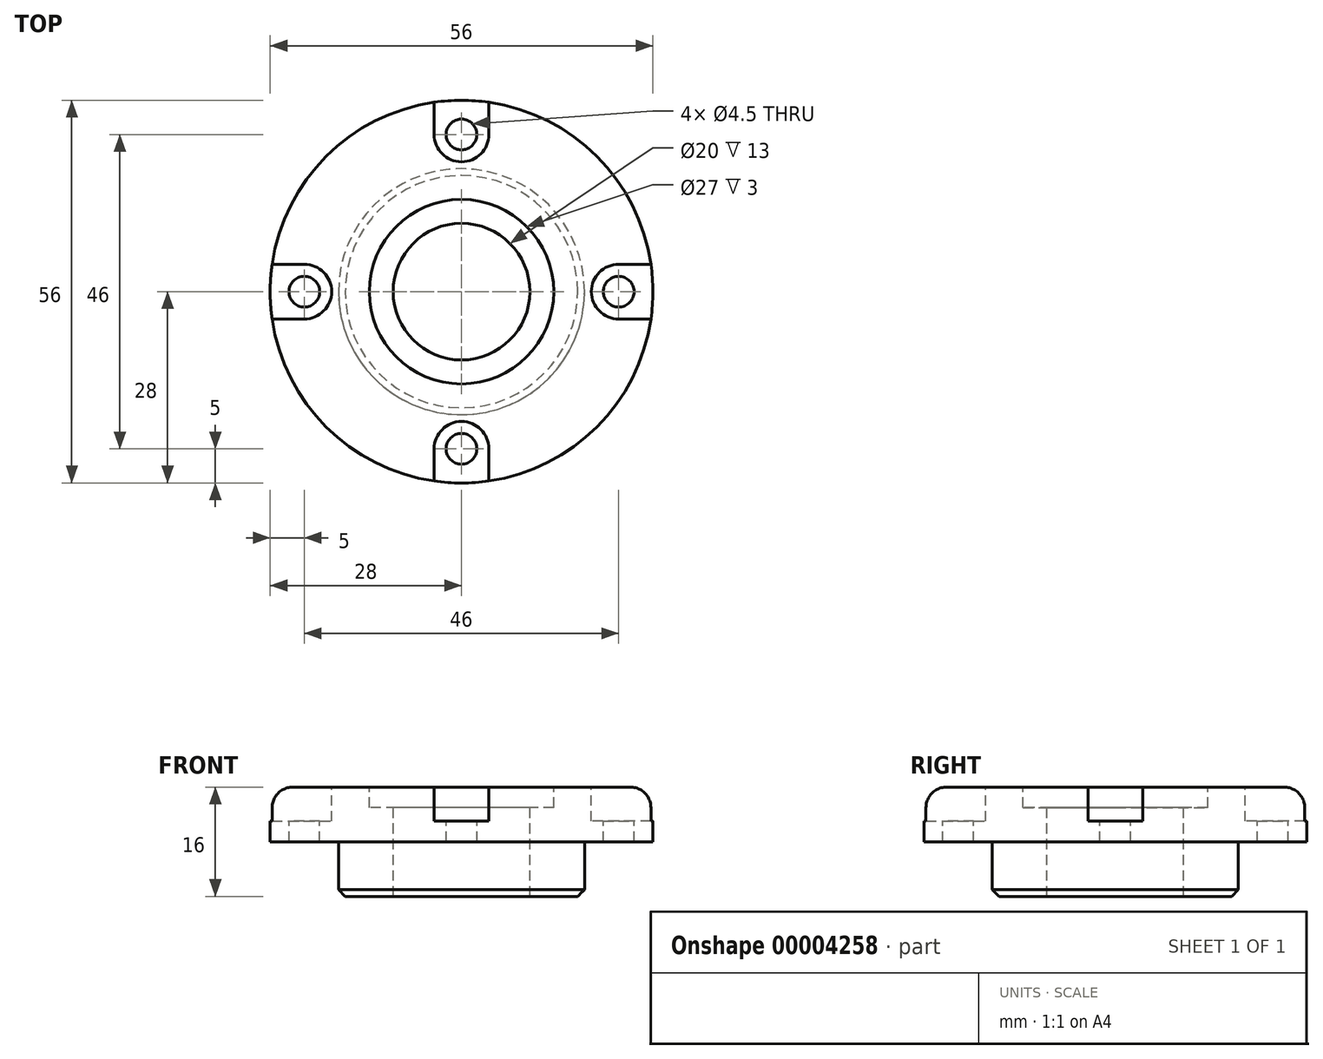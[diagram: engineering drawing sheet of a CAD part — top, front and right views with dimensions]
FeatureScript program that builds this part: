
annotation { "Feature Type Name" : "Feature", "Feature Type Description" : "" }
export const myFeature = defineFeature(function(context is Context, id is Id, definition is map)
    precondition{}
    {
        {
            var Q0;
            Q0=qCreatedBy(makeId("Front.planeOp"),FACE);
            var sketch = newSketch(context, id + "F0", { "sketchPlane" : qUnion([Q0])});
            skLineSegment(sketch, "E0", {"start": v(0, 0) * mm, "end": v(0, 33.62) * mm, "construction": true});
            skLineSegment(sketch, "E1", {"start": v(0, 16) * mm, "end": v(28, 16) * mm});
            skLineSegment(sketch, "E2", {"start": v(28, 16) * mm, "end": v(28, 8) * mm});
            skLineSegment(sketch, "E3", {"start": v(28, 8) * mm, "end": v(18, 8) * mm});
            skLineSegment(sketch, "E4", {"start": v(18, 8) * mm, "end": v(18, 0) * mm});
            skLineSegment(sketch, "E5", {"start": v(18, 0) * mm, "end": v(0, 0) * mm});
            skLineSegment(sketch, "E6", {"start": v(0, 16) * mm, "end": v(0, 0) * mm});
            skSolve(sketch);
        }
        {
            var Q0;
            Q0 = qSketchRegion(id + "F0", true);
            var Q1;
            Q1=sQuery(id+"F0.wireOp",EDGE,"E0");
            revolve(context, id + "F1", {"entities" : qUnion([Q0]), "axis" : qUnion([Q1]), "revolveType" : RevolveType.FULL});
        }
        {
            var Q0;
            Q0=qCreatedBy(makeId("Front.planeOp"),FACE);
            var sketch = newSketch(context, id + "F2", { "sketchPlane" : qUnion([Q0])});
            skLineSegment(sketch, "E7", {"start": v(0, 0) * mm, "end": v(0, 20.28) * mm, "construction": true});
            skLineSegment(sketch, "E8", {"start": v(0, 16) * mm, "end": v(13.5, 16) * mm});
            skLineSegment(sketch, "E9", {"start": v(13.5, 16) * mm, "end": v(13.5, 13) * mm});
            skLineSegment(sketch, "E10", {"start": v(13.5, 13) * mm, "end": v(10, 13) * mm});
            skLineSegment(sketch, "E11", {"start": v(10, 13) * mm, "end": v(10, 0) * mm});
            skLineSegment(sketch, "E12", {"start": v(10, 0) * mm, "end": v(0, 0) * mm});
            skLineSegment(sketch, "E13", {"start": v(0, 0) * mm, "end": v(0, 16) * mm});
            skSolve(sketch);
        }
        {
            var Q0;
            Q0 = qSketchRegion(id + "F2", true);
            var Q1;
            Q1=sQuery(id+"F2.wireOp",EDGE,"E7");
            revolve(context, id + "F3", {"operationType" : NewBodyOperationType.REMOVE, "entities" : qUnion([Q0]), "axis" : qUnion([Q1]), "revolveType" : RevolveType.FULL, "oppositeDirection" : true});
        }
        {
            var Q0;
            Q0=makeQuery(id+"F1.opRevolve","SWEPT_FACE",FACE,{"disambiguationData":[OSD([sQuery(id+"F0.wireOp",EDGE,"E1")])]});
            var sketch = newSketch(context, id + "F4", { "sketchPlane" : qUnion([Q0])});
            skLineSegment(sketch, "E14", {"start": v(-4, 27.71) * mm, "end": v(-4, 23) * mm});
            skLineSegment(sketch, "E15", {"start": v(4, 27.71) * mm, "end": v(4, 23) * mm});
            skArc(sketch, "E16", {"start": v(-4, 23) * mm, "mid": v(0, 19) * mm, "end": v(4, 23) * mm});
            skArc(sketch, "E17.0", {"start": v(4, 27.71) * mm, "mid": v(0, 28) * mm, "end": v(-4, 27.71) * mm});
            skLineSegment(sketch, "E18", {"start": v(0, 0) * mm, "end": v(0, 23) * mm, "construction": true});
            skCircle(sketch, "E19", {"center": v(0, 0) * mm, "radius": 23 * mm, "construction": true});
            skSolve(sketch);
        }
        {
            var Q0;
            Q0=makeQuery(id+"F1.opRevolve","SWEPT_EDGE",EDGE,{"disambiguationData":[OSD([sQuery(id+"F0.wireOp",EDGE,"E1"),sQuery(id+"F0.wireOp",EDGE,"E2")])]});
            fillet(context, id + "F5", {"entities" : qUnion([Q0]), "radius" : 3 * mm, "tangentPropagation" : true, "allowEdgeOverflow" : false});
        }
        {
            var Q0;
            Q0=makeQuery(id+"F4.imprint","IMPRINT",FACE,{"disambiguationData":[TD([[makeQuery(id+"F4.imprint","IMPRINT",EDGE,{"derivedFrom":sQuery(id+"F4.wireOp",EDGE,"E14")}),1.0]])]});
            extrude(context, id + "F6", {"entities" : qUnion([Q0]), "operationType" : NewBodyOperationType.REMOVE, "oppositeDirection" : true, "depth" : 5 * mm});
        }
        {
            var Q0;
            Q0=makeQuery(id+"F6.boolean.opBoolean","COPY",FACE,{"derivedFrom":makeQuery(id+"F6.opExtrude","SWEPT_FACE",FACE,{"disambiguationData":[OSD([sQuery(id+"F4.wireOp",EDGE,"E16")])]})});
            var Q1;
            Q1=makeQuery(id+"F6.boolean.opBoolean","COPY",FACE,{"derivedFrom":makeQuery(id+"F6.opExtrude","SWEPT_FACE",FACE,{"disambiguationData":[OSD([sQuery(id+"F4.wireOp",EDGE,"E14")])]})});
            var Q2;
            Q2=makeQuery(id+"F6.boolean.opBoolean","COPY",FACE,{"derivedFrom":makeQuery(id+"F6.opExtrude","CAP_FACE",FACE,{"disambiguationData":[OSD([sQuery(id+"F4.wireOp",EDGE,"E14"),sQuery(id+"F4.wireOp",EDGE,"E15"),sQuery(id+"F4.wireOp",EDGE,"E16"),sQuery(id+"F4.wireOp",EDGE,"E17.0")])],"isStart":false})});
            var Q3;
            Q3=makeQuery(id+"F6.boolean.opBoolean","COPY",FACE,{"derivedFrom":makeQuery(id+"F6.opExtrude","SWEPT_FACE",FACE,{"disambiguationData":[OSD([sQuery(id+"F4.wireOp",EDGE,"E15")])]})});
            var Q4;
            Q4=makeQuery(id+"F3.boolean.opBoolean","COPY",FACE,{"derivedFrom":makeQuery(id+"F3.opRevolve","SWEPT_FACE",FACE,{"disambiguationData":[OSD([sQuery(id+"F2.wireOp",EDGE,"E11")])]})});
            circularPattern(context, id + "F7", {"faces" : qUnion([Q0, Q1, Q2, Q3]), "axis" : qUnion([Q4]), "angle" : 360 * degree, "instanceCount" : 4, "equalSpace" : true, "patternType" : PatternType.FACE});
        }
        {
            var Q0;
            Q0=makeQuery(id+"F6.boolean.opBoolean","COPY",FACE,{"derivedFrom":makeQuery(id+"F6.opExtrude","CAP_FACE",FACE,{"disambiguationData":[OSD([sQuery(id+"F4.wireOp",EDGE,"E14"),sQuery(id+"F4.wireOp",EDGE,"E15"),sQuery(id+"F4.wireOp",EDGE,"E16"),sQuery(id+"F4.wireOp",EDGE,"E17.0")])],"isStart":false})});
            var sketch = newSketch(context, id + "F8", { "sketchPlane" : qUnion([Q0])});
            skCircle(sketch, "E20", {"center": v(0, 23) * mm, "radius": 2.25 * mm});
            skSolve(sketch);
        }
        {
            var Q0;
            Q0 = qSketchRegion(id + "F8", true);
            extrude(context, id + "F9", {"entities" : qUnion([Q0]), "operationType" : NewBodyOperationType.REMOVE, "endBound" : BoundingType.THROUGH_ALL, "oppositeDirection" : true, "depth" : 25 * mm});
        }
        {
            var Q0;
            Q0=makeQuery(id+"F9.boolean.opBoolean","COPY",FACE,{"derivedFrom":makeQuery(id+"F9.opExtrude","SWEPT_FACE",FACE,{"disambiguationData":[OSD([sQuery(id+"F8.wireOp",EDGE,"E20")])]})});
            var Q1;
            Q1=makeQuery(id+"F3.boolean.opBoolean","COPY",FACE,{"derivedFrom":makeQuery(id+"F3.opRevolve","SWEPT_FACE",FACE,{"disambiguationData":[OSD([sQuery(id+"F2.wireOp",EDGE,"E11")])]})});
            circularPattern(context, id + "F10", {"faces" : qUnion([Q0]), "axis" : qUnion([Q1]), "angle" : 360 * degree, "instanceCount" : 4, "equalSpace" : true, "patternType" : PatternType.FACE});
        }
        {
            var Q0;
            Q0=makeQuery(id+"F1.opRevolve","SWEPT_EDGE",EDGE,{"disambiguationData":[OSD([sQuery(id+"F0.wireOp",EDGE,"E4"),sQuery(id+"F0.wireOp",EDGE,"E5")])]});
            chamfer(context, id + "F11", {"entities" : qUnion([Q0]), "width" : 1 * mm, "tangentPropagation" : true});
        }
    });
